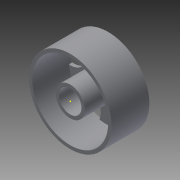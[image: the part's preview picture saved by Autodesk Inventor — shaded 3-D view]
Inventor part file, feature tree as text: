
AUTODESK INVENTOR PART (.ipt)
format: ipt  version: 2015 (Build 190159000, 159)  size: 136,704 bytes
history: native  units: in
note: dims shown in document units (in); Inventor stores cm internally (conversion verified against a paired STEP export)
features: sketch x3, extrude x3
ambient origin geometry x8: Origin, YZ Plane, XZ Plane, XY Plane, X Axis, Y Axis, Z Axis, Center Point
bodies: Solid1 (feature_tree)
feature tree (6):
  sketch  "Sketch1"  dims[d0=0.05in d1=0.44in]
  extrude  "Extrusion1"  Depth=0.05in
  sketch  "Sketch3"  dims[d2=0.05in d3=0.35in]
  extrude  "Extrusion2"  Depth=0.05in
  extrude  "Extrusion3"  Depth=0.05in TaperAngle=0.0deg
  sketch  "Sketch4"  dims[d4=0.57in d5=0.0in d6=0.05in d7=0.0in d8=0.5in d9=1.9685in d11=360.0deg d13=0.1in d14=0.0in]
